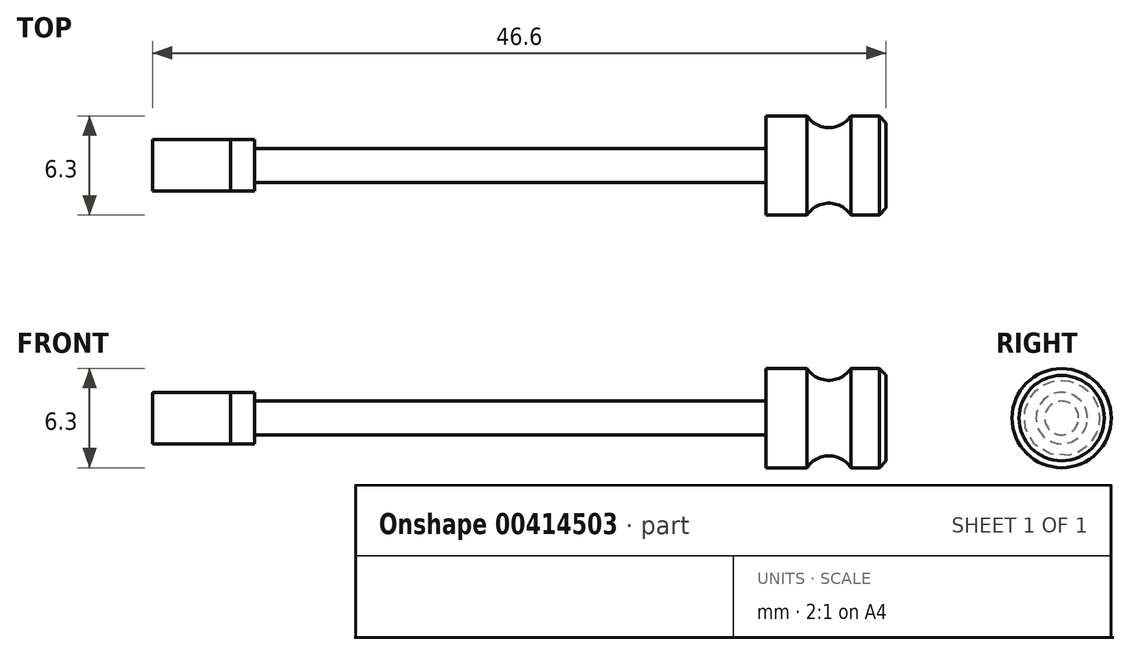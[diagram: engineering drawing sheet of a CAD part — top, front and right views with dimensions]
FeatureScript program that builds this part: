
annotation { "Feature Type Name" : "Feature", "Feature Type Description" : "" }
export const myFeature = defineFeature(function(context is Context, id is Id, definition is map)
    precondition{}
    {
        {
            var Q0;
            Q0=qCreatedBy(makeId("Front.planeOp"),FACE);
            var sketch = newSketch(context, id + "F0", { "sketchPlane" : qUnion([Q0])});
            skLineSegment(sketch, "E0.bottom", {"start": v(-16.4, 0) * mm, "end": v(25.23, 0) * mm});
            skLineSegment(sketch, "E0.top", {"start": v(-14.89, 1.07) * mm, "end": v(17.6, 1.07) * mm});
            skLineSegment(sketch, "E1.top", {"start": v(17.6, 3.15) * mm, "end": v(20.2, 3.15) * mm});
            skLineSegment(sketch, "E1.left", {"start": v(17.6, 1.07) * mm, "end": v(17.6, 3.15) * mm});
            skLineSegment(sketch, "E1.right", {"start": v(25.23, 0) * mm, "end": v(25.23, 2.7) * mm});
            skArc(sketch, "E2", {"start": v(20.2, 3.15) * mm, "mid": v(21.6, 2.4) * mm, "end": v(22.98, 3.15) * mm});
            skLineSegment(sketch, "E3.trimOffspring", {"start": v(22.98, 3.15) * mm, "end": v(24.8, 3.15) * mm});
            skLineSegment(sketch, "E4", {"start": v(24.8, 3.15) * mm, "end": v(25.23, 2.7) * mm});
            skLineSegment(sketch, "E5.top", {"start": v(-14.89, 1.63) * mm, "end": v(-16.4, 1.63) * mm});
            skLineSegment(sketch, "E5.left", {"start": v(-14.89, 1.07) * mm, "end": v(-14.89, 1.63) * mm});
            skLineSegment(sketch, "E5.right", {"start": v(-16.4, 0) * mm, "end": v(-16.4, 1.63) * mm});
            skLineSegment(sketch, "E6", {"start": v(21.6, 4.06) * mm, "end": v(21.6, 0) * mm, "construction": true});
            skPoint(sketch, "E6.endSnap0", {"position": v(21.6, 2.4) * mm});
            skSolve(sketch);
        }
        {
            var Q0;
            Q0 = qSketchRegion(id + "F0", true);
            var Q1;
            Q1=sQuery(id+"F0.wireOp",EDGE,"E0.bottom");
            revolve(context, id + "F1", {"entities" : qUnion([Q0]), "axis" : qUnion([Q1]), "revolveType" : RevolveType.ONE_DIRECTION, "angle" : 360 * degree});
        }
        {
            var Q0;
            Q0=makeQuery(id+"F1.opRevolve","SWEPT_FACE",FACE,{"disambiguationData":[OSD([sQuery(id+"F0.wireOp",EDGE,"E5.right")])]});
            var sketch = newSketch(context, id + "F2", { "sketchPlane" : qUnion([Q0])});
            skCircle(sketch, "E7", {"center": v(0, 0) * mm, "radius": 1.63 * mm});
            skSolve(sketch);
        }
        {
            var Q0;
            Q0 = qSketchRegion(id + "F2", true);
            extrude(context, id + "F3", {"entities" : qUnion([Q0]), "depth" : 4.97 * mm});
        }
    });
